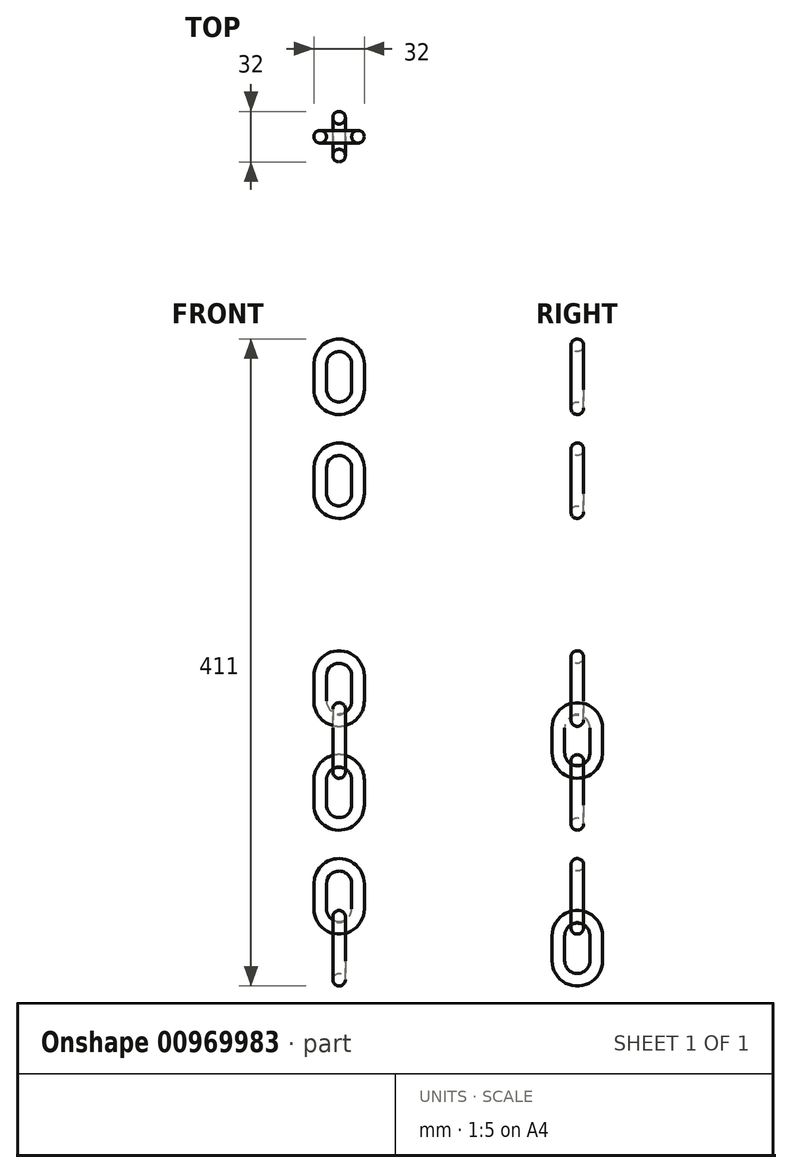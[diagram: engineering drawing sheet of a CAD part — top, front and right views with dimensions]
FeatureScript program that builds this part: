
annotation { "Feature Type Name" : "Feature", "Feature Type Description" : "" }
export const myFeature = defineFeature(function(context is Context, id is Id, definition is map)
    precondition{}
    {
        {
            var Q0;
            Q0=qCreatedBy(makeId("Top.planeOp"),FACE);
            var sketch = newSketch(context, id + "F0", { "sketchPlane" : qUnion([Q0])});
            skCircle(sketch, "E0", {"center": v(0, 12) * mm, "radius": 4 * mm});
            skSolve(sketch);
        }
        {
            var Q0;
            Q0=qCreatedBy(makeId("Right.planeOp"),FACE);
            var sketch = newSketch(context, id + "F1", { "sketchPlane" : qUnion([Q0])});
            skLineSegment(sketch, "E1.bottom", {"start": v(-12, -8) * mm, "end": v(12, -8) * mm, "construction": true});
            skLineSegment(sketch, "E1.top", {"start": v(-12, 8) * mm, "end": v(12, 8) * mm, "construction": true});
            skLineSegment(sketch, "E1.left", {"start": v(-12, -8) * mm, "end": v(-12, 8) * mm});
            skLineSegment(sketch, "E1.right", {"start": v(12, -8) * mm, "end": v(12, 8) * mm});
            skLineSegment(sketch, "E2", {"start": v(-12, -8) * mm, "end": v(0, 0) * mm, "construction": true});
            skLineSegment(sketch, "E3", {"start": v(0, 0) * mm, "end": v(12, -8) * mm, "construction": true});
            skArc(sketch, "E4", {"start": v(-12, -8) * mm, "mid": v(0, -20) * mm, "end": v(12, -8) * mm});
            skLineSegment(sketch, "E5", {"start": v(0, 0) * mm, "end": v(-12, 0) * mm, "construction": true});
            skArc(sketch, "E6.MirrorCS", {"start": v(-12, 8) * mm, "mid": v(0, 20) * mm, "end": v(12, 8) * mm});
            skSolve(sketch);
        }
        {
            var Q0;
            Q0=makeQuery(id+"F0.imprint","IMPRINT",FACE,{"disambiguationData":[TD([[makeQuery(id+"F0.imprint","IMPRINT",EDGE,{"derivedFrom":sQuery(id+"F0.wireOp",EDGE,"E0")}),1.0]])]});
            var Q1;
            Q1=sQuery(id+"F1.wireOp",EDGE,"E1.right");
            var Q2;
            Q2=sQuery(id+"F1.wireOp",EDGE,"E4");
            var Q3;
            Q3=sQuery(id+"F1.wireOp",EDGE,"E1.left");
            var Q4;
            Q4=sQuery(id+"F1.wireOp",EDGE,"E6.MirrorCS");
            sweep(context, id + "F2", {"profiles" : qUnion([Q0]), "path" : qUnion([Q1, Q2, Q3, Q4])});
        }
        {
            var Q0;
            Q0=makeQuery(id+"F2.opSweep","SWEPT_BODY",BODY,{"disambiguationData":[OSD([sQuery(id+"F0.wireOp",EDGE,"E0"),sQuery(id+"F1.wireOp",EDGE,"E4")])]});
            transform(context, id + "F3", {"entities" : qUnion([Q0]), "transformType" : TransformType.TRANSLATION_3D, "dx" : 0 * mm, "dy" : 0 * mm, "dz" : 33 * mm, "makeCopy" : true});
        }
        {
            var Q0;
            Q0=qCreatedBy(makeId("Right.planeOp"),FACE);
            var sketch = newSketch(context, id + "F4", { "sketchPlane" : qUnion([Q0])});
            skLineSegment(sketch, "E7", {"start": v(0, 0) * mm, "end": v(0, 71.54) * mm, "construction": true});
            skSolve(sketch);
        }
        {
            var Q0;
            Q0=makeQuery(id+"F3.opPattern","COPY",BODY,{"derivedFrom":makeQuery(id+"F2.opSweep","SWEPT_BODY",BODY,{"disambiguationData":[OSD([sQuery(id+"F0.wireOp",EDGE,"E0"),sQuery(id+"F1.wireOp",EDGE,"E4")])]}),"instanceName":"1"});
            var Q1;
            Q1=sQuery(id+"F4.wireOp",EDGE,"E7");
            transform(context, id + "F5", {"entities" : qUnion([Q0]), "transformType" : TransformType.ROTATION, "transformAxis" : qUnion([Q1]), "angle" : 90 * degree, "makeCopy" : false});
        }
        {
            var Q0;
            Q0=makeQuery(id+"F3.opPattern","COPY",BODY,{"derivedFrom":makeQuery(id+"F2.opSweep","SWEPT_BODY",BODY,{"disambiguationData":[OSD([sQuery(id+"F0.wireOp",EDGE,"E0"),sQuery(id+"F1.wireOp",EDGE,"E4")])]}),"instanceName":"1"});
            transform(context, id + "F6", {"entities" : qUnion([Q0]), "transformType" : TransformType.TRANSLATION_3D, "dx" : 0 * mm, "dy" : 0 * mm, "dz" : 66 * mm, "makeCopy" : true});
        }
        {
            var Q0;
            Q0=makeQuery(id+"F3.opPattern","COPY",BODY,{"derivedFrom":makeQuery(id+"F2.opSweep","SWEPT_BODY",BODY,{"disambiguationData":[OSD([sQuery(id+"F0.wireOp",EDGE,"E0"),sQuery(id+"F1.wireOp",EDGE,"E4")])]}),"instanceName":"1"});
            transform(context, id + "F7", {"entities" : qUnion([Q0]), "transformType" : TransformType.TRANSLATION_3D, "dx" : 0 * mm, "dy" : 0 * mm, "dz" : 132 * mm, "makeCopy" : true});
        }
        {
            var Q0;
            Q0=makeQuery(id+"F3.opPattern","COPY",BODY,{"derivedFrom":makeQuery(id+"F2.opSweep","SWEPT_BODY",BODY,{"disambiguationData":[OSD([sQuery(id+"F0.wireOp",EDGE,"E0"),sQuery(id+"F1.wireOp",EDGE,"E4")])]}),"instanceName":"1"});
            transform(context, id + "F8", {"entities" : qUnion([Q0]), "transformType" : TransformType.TRANSLATION_3D, "dx" : 0 * mm, "dy" : 0 * mm, "dz" : 66 * mm, "makeCopy" : true});
        }
        {
            var Q0;
            Q0=makeQuery(id+"F3.opPattern","COPY",BODY,{"derivedFrom":makeQuery(id+"F2.opSweep","SWEPT_BODY",BODY,{"disambiguationData":[OSD([sQuery(id+"F0.wireOp",EDGE,"E0"),sQuery(id+"F1.wireOp",EDGE,"E4")])]}),"instanceName":"1"});
            var Q1;
            Q1=makeQuery(id+"F8.opPattern","COPY",BODY,{"derivedFrom":makeQuery(id+"F3.opPattern","COPY",BODY,{"derivedFrom":makeQuery(id+"F2.opSweep","SWEPT_BODY",BODY,{"disambiguationData":[OSD([sQuery(id+"F0.wireOp",EDGE,"E0"),sQuery(id+"F1.wireOp",EDGE,"E4")])]}),"instanceName":"1"}),"instanceName":"1"});
            booleanBodies(context, id + "F9", {"operationType" : BooleanOperationType.SUBTRACTION, "tools" : qUnion([Q0]), "targets" : qUnion([Q1]), "keepTools" : true});
        }
        {
            var Q0;
            Q0=makeQuery(id+"F8.opPattern","COPY",BODY,{"derivedFrom":makeQuery(id+"F3.opPattern","COPY",BODY,{"derivedFrom":makeQuery(id+"F2.opSweep","SWEPT_BODY",BODY,{"disambiguationData":[OSD([sQuery(id+"F0.wireOp",EDGE,"E0"),sQuery(id+"F1.wireOp",EDGE,"E4")])]}),"instanceName":"1"}),"instanceName":"1"});
            transform(context, id + "F10", {"entities" : qUnion([Q0]), "transformType" : TransformType.TRANSLATION_3D, "dx" : 0 * mm, "dy" : 0 * mm, "dz" : 33 * mm, "makeCopy" : true});
        }
        {
            var Q0;
            Q0=makeQuery(id+"F10.opPattern","COPY",BODY,{"derivedFrom":makeQuery(id+"F8.opPattern","COPY",BODY,{"derivedFrom":makeQuery(id+"F3.opPattern","COPY",BODY,{"derivedFrom":makeQuery(id+"F2.opSweep","SWEPT_BODY",BODY,{"disambiguationData":[OSD([sQuery(id+"F0.wireOp",EDGE,"E0"),sQuery(id+"F1.wireOp",EDGE,"E4")])]}),"instanceName":"1"}),"instanceName":"1"}),"instanceName":"1"});
            var Q1;
            Q1=sQuery(id+"F4.wireOp",EDGE,"E7");
            transform(context, id + "F11", {"entities" : qUnion([Q0]), "transformType" : TransformType.ROTATION, "transformAxis" : qUnion([Q1]), "angle" : 90 * degree, "makeCopy" : false});
        }
        {
            var Q0;
            Q0=makeQuery(id+"F3.opPattern","COPY",BODY,{"derivedFrom":makeQuery(id+"F2.opSweep","SWEPT_BODY",BODY,{"disambiguationData":[OSD([sQuery(id+"F0.wireOp",EDGE,"E0"),sQuery(id+"F1.wireOp",EDGE,"E4")])]}),"instanceName":"1"});
            transform(context, id + "F12", {"entities" : qUnion([Q0]), "transformType" : TransformType.TRANSLATION_3D, "dx" : 0 * mm, "dy" : 0 * mm, "dz" : 132 * mm, "makeCopy" : true});
        }
        {
            var Q0;
            Q0=makeQuery(id+"F3.opPattern","COPY",BODY,{"derivedFrom":makeQuery(id+"F2.opSweep","SWEPT_BODY",BODY,{"disambiguationData":[OSD([sQuery(id+"F0.wireOp",EDGE,"E0"),sQuery(id+"F1.wireOp",EDGE,"E4")])]}),"instanceName":"1"});
            transform(context, id + "F13", {"entities" : qUnion([Q0]), "transformType" : TransformType.TRANSLATION_3D, "dx" : 0 * mm, "dy" : 0 * mm, "dz" : 330 * mm, "makeCopy" : true});
        }
        {
            var Q0;
            Q0=makeQuery(id+"F3.opPattern","COPY",BODY,{"derivedFrom":makeQuery(id+"F2.opSweep","SWEPT_BODY",BODY,{"disambiguationData":[OSD([sQuery(id+"F0.wireOp",EDGE,"E0"),sQuery(id+"F1.wireOp",EDGE,"E4")])]}),"instanceName":"1"});
            transform(context, id + "F14", {"entities" : qUnion([Q0]), "transformType" : TransformType.TRANSLATION_3D, "dx" : 0 * mm, "dy" : 0 * mm, "dz" : 264 * mm, "makeCopy" : true});
        }
    });
